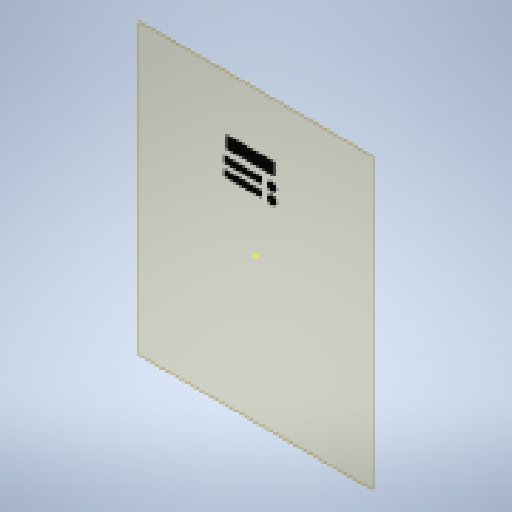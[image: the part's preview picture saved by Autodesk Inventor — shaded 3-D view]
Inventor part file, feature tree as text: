
AUTODESK INVENTOR PART (.ipt)
format: ipt  version: 2023 (Build 270158030, 158C)  size: 187,904 bytes
history: native  units: mm
features: other x4, sketch x2, plane x1, extrude x1
ambient origin geometry x8: Origin, YZ Plane, XZ Plane, XY Plane, X Axis, Y Axis, Z Axis, Center Point
bodies: Solid1 (feature_tree)
feature tree (8):
  plane  "Work Plane1"
  extrude  "Extrusion1"  Depth=12.0mm
  sketch  "Sketch2"  dims[d2=70.0mm d3=12.0mm d4=16.0mm d5=20.0mm d8=20.0mm d9=1.0mm d10=0.0mm d11=23.0mm d12=90.0mm d13=5.0mm]
  sketch  "Sketch1"  dims[d0=70.0mm d1=12.0mm]
  other  "Image1"
  other  "<userpath>\Documents\0004-inventor\Inventor_Projects\electronics-enclosure\enclosure.iam"
  other  "enclosure.iam"
  other  "door:1"
